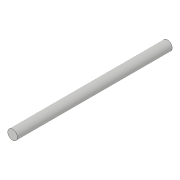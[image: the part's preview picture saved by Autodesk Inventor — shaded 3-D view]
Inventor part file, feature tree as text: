
AUTODESK INVENTOR PART (.ipt)
format: ipt  version: 2018 (Build 220112000, 112)  size: 70,144 bytes
history: native  units: in
note: dims shown in document units (in); Inventor stores cm internally (conversion verified against a paired STEP export)
features: extrude x1, sketch x1
ambient origin geometry x8: Origin, YZ Plane, XZ Plane, XY Plane, X Axis, Y Axis, Z Axis, Center Point
bodies: Solid1 (feature_tree)
feature tree (2):
  extrude  "Extrusion1"  Depth=8.0in TaperAngle=0.0deg
  sketch  "Sketch1"  dims[d0=0.5in d1=8.0in d2=0.0in]
